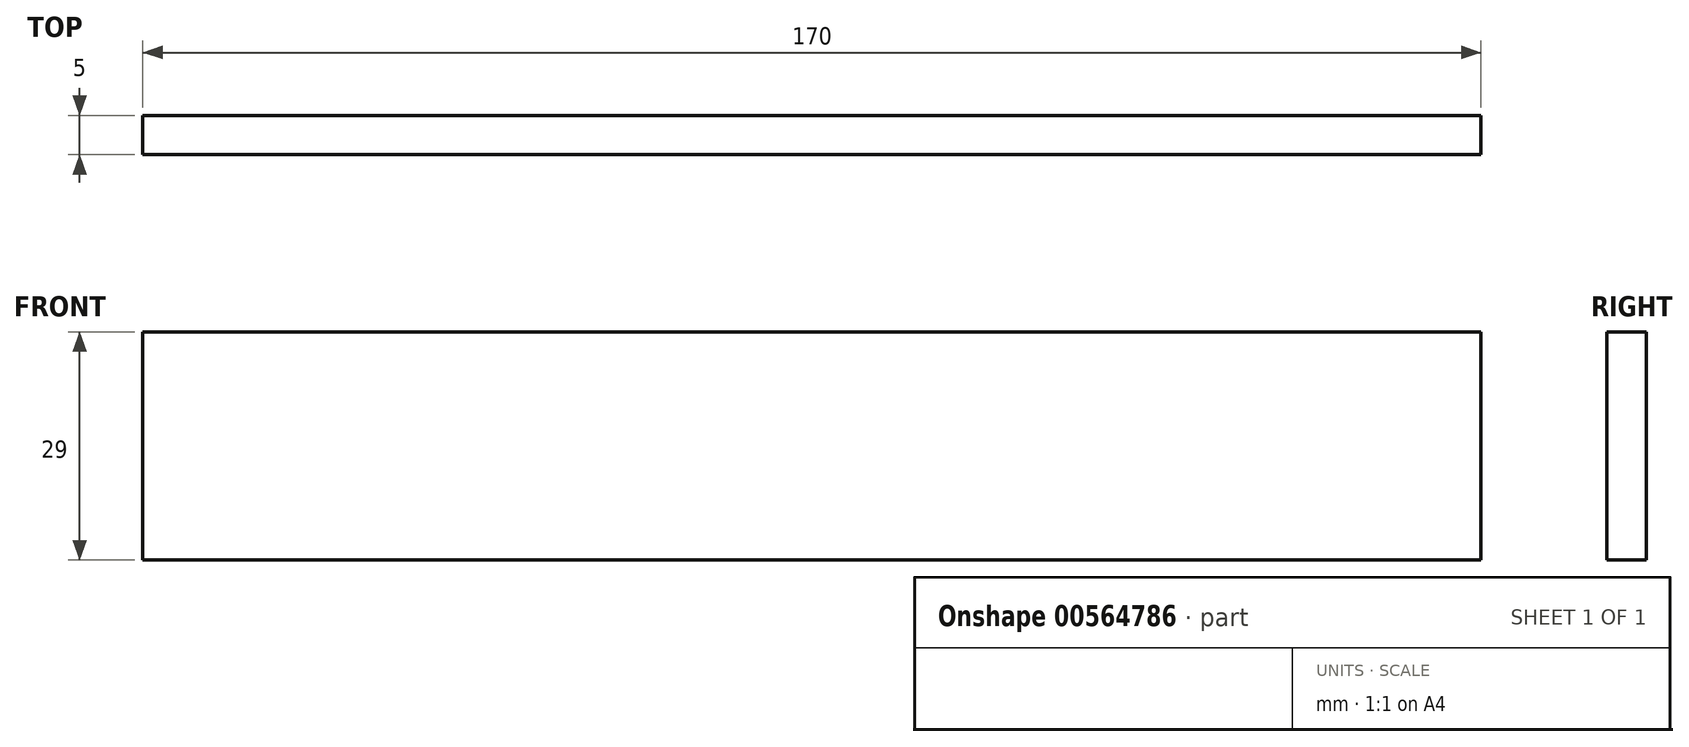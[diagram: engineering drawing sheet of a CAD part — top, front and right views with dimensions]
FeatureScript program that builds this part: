
annotation { "Feature Type Name" : "Feature", "Feature Type Description" : "" }
export const myFeature = defineFeature(function(context is Context, id is Id, definition is map)
    precondition{}
    {
        {
            var Q0;
            Q0=qCreatedBy(makeId("Front.planeOp"),FACE);
            var sketch = newSketch(context, id + "F0", { "sketchPlane" : qUnion([Q0])});
            skLineSegment(sketch, "E0.bottom", {"start": v(-85, 14.5) * mm, "end": v(85, 14.5) * mm});
            skLineSegment(sketch, "E0.top", {"start": v(-85, -14.5) * mm, "end": v(85, -14.5) * mm});
            skLineSegment(sketch, "E0.left", {"start": v(-85, 14.5) * mm, "end": v(-85, -14.5) * mm});
            skLineSegment(sketch, "E0.right", {"start": v(85, 14.5) * mm, "end": v(85, -14.5) * mm});
            skPoint(sketch, "E0.middle", {"position": v(0, 0) * mm});
            skSolve(sketch);
        }
        {
            var Q0;
            Q0 = qSketchRegion(id + "F0", true);
            extrude(context, id + "F1", {"entities" : qUnion([Q0]), "depth" : 5 * mm, "offsetDistance" : 25 * mm});
        }
    });
